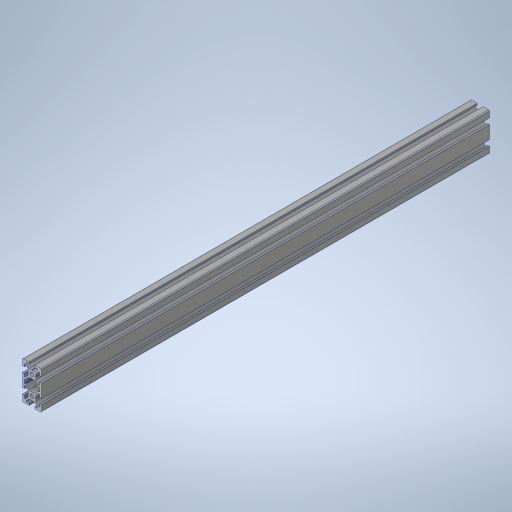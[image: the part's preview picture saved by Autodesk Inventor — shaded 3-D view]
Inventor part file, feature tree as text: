
AUTODESK INVENTOR PART (.ipt)
format: ipt  version: 2024 (Build 280153000, 153)  size: 462,336 bytes
history: native  units: mm
features: other x7, sketch x2, extrude x1, hole x1, pattern_linear x1, mirror x1
ambient origin geometry x8: Origin, YZ Plane, XZ Plane, XY Plane, X Axis, Y Axis, Z Axis, Center Point
bodies: Solid1 (feature_tree)
feature tree (13):
  extrude  "Extrusion1"  Depth=20.0mm TaperAngle=0.0deg
  hole  "Hole1"  [1 undecoded]
  pattern_linear  "Rectangular Pattern1"  [2 undecoded]
  other  "C1_XY"
  other  "C1_YZ"
  other  "C1_ZX"
  other  "C1_X"
  other  "C1_Y"
  other  "C1_Z"
  other  "C1_Center"
  mirror  "Mirror1"
  sketch  "Sketch_1"  dims[d0=475.0mm d1=0.0mm]
  sketch  "Sketch2"  dims[d2=4.134mm d3=10.0mm d4=4.0mm d5=2.0mm d6=90.0deg d7=500.0mm d8=0.0mm d9=20.0mm d11=20.0mm d12=10.0mm d14=0.0mm d15=0.0mm]
note: 3 required parameter values undecoded (feature->parameter linkage not recoverable at this tier; creation-order binding heuristic only, values carry confidence <= 0.55)
